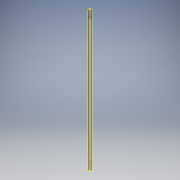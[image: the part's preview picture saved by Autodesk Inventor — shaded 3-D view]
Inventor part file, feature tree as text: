
AUTODESK INVENTOR PART (.ipt)
format: ipt  version: 2018 (Build 220112000, 112)  size: 104,448 bytes
history: native  units: mm
features: other x6, extrude x1, sketch x1
ambient origin geometry x8: Origin, YZ Plane, XZ Plane, XY Plane, X Axis, Y Axis, Z Axis, Center Point
bodies: Body1 (feature_tree)
feature tree (8):
  extrude  "押し出し2"  Depth=27.2mm
  other  "面の勾配1"
  other  "面の勾配2"
  other  "作業平面2"
  other  "作業平面4"
  other  "作業平面5"
  other  "作業平面6"
  sketch  "スケッチ3"
